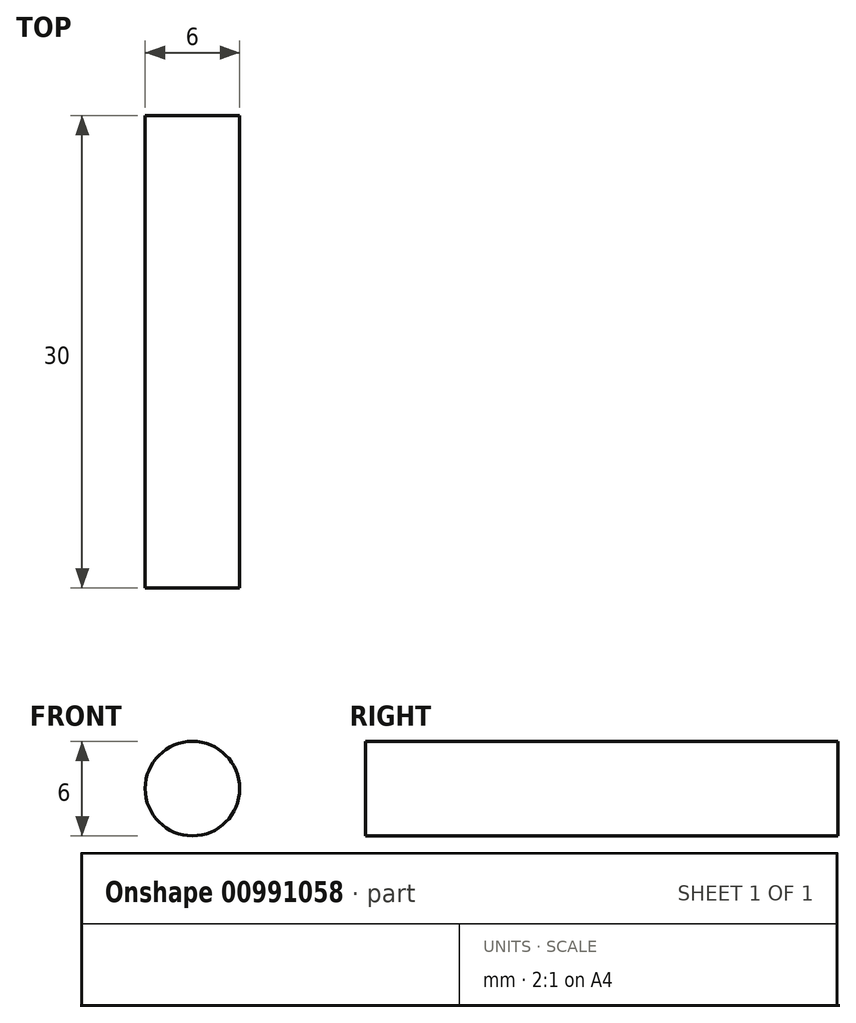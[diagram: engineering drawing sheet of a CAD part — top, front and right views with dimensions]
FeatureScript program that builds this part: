
annotation { "Feature Type Name" : "Feature", "Feature Type Description" : "" }
export const myFeature = defineFeature(function(context is Context, id is Id, definition is map)
    precondition{}
    {
        {
            var Q0;
            Q0=qCreatedBy(makeId("Front.planeOp"),FACE);
            var sketch = newSketch(context, id + "F0", { "sketchPlane" : qUnion([Q0])});
            skCircle(sketch, "E0", {"center": v(-9.35, 4.87) * mm, "radius": 3 * mm});
            skSolve(sketch);
        }
        {
            var Q0;
            Q0=makeQuery(id+"F0.imprint","IMPRINT",FACE,{"disambiguationData":[TD([[makeQuery(id+"F0.imprint","IMPRINT",EDGE,{"derivedFrom":sQuery(id+"F0.wireOp",EDGE,"E0")}),1.0]])]});
            extrude(context, id + "F1", {"entities" : qUnion([Q0]), "depth" : 30 * mm, "offsetDistance" : 25.4 * mm});
        }
    });
